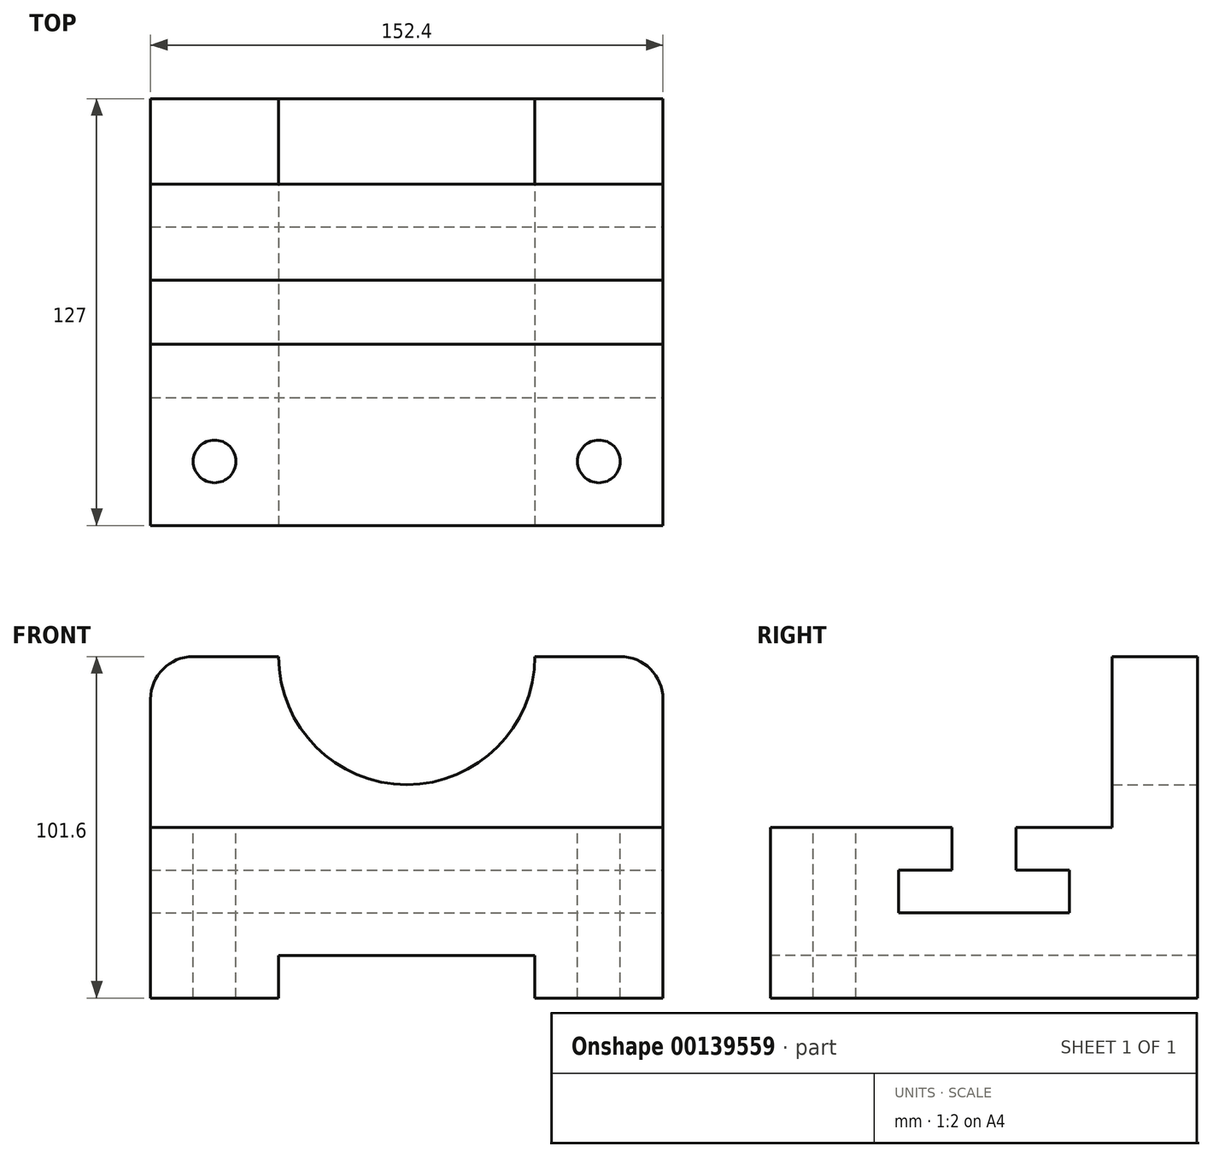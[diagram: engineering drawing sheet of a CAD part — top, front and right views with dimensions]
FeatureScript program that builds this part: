
annotation { "Feature Type Name" : "Feature", "Feature Type Description" : "" }
export const myFeature = defineFeature(function(context is Context, id is Id, definition is map)
    precondition{}
    {
        {
            var Q0;
            Q0=qCreatedBy(makeId("Front.planeOp"),FACE);
            var sketch = newSketch(context, id + "F0", { "sketchPlane" : qUnion([Q0])});
            skLineSegment(sketch, "E0", {"start": v(0, 0) * mm, "end": v(76.2, 0) * mm});
            skLineSegment(sketch, "E1.MirrorCS", {"start": v(0, 0) * mm, "end": v(-76.2, 0) * mm});
            skLineSegment(sketch, "E2", {"start": v(-76.2, 0) * mm, "end": v(-76.2, 101.6) * mm});
            skLineSegment(sketch, "E3.MirrorCS", {"start": v(76.2, 0) * mm, "end": v(76.2, 101.6) * mm});
            skLineSegment(sketch, "E4", {"start": v(-76.2, 101.6) * mm, "end": v(76.2, 101.6) * mm});
            skSolve(sketch);
        }
        {
            var Q0;
            Q0 = qSketchRegion(id + "F0", true);
            extrude(context, id + "F1", {"entities" : qUnion([Q0]), "endBound" : BoundingType.SYMMETRIC, "oppositeDirection" : true, "depth" : 127 * mm});
        }
        {
            var Q0;
            Q0=makeQuery(id+"F1.opExtrude","CAP_FACE",FACE,{"disambiguationData":[OSD([sQuery(id+"F0.wireOp",EDGE,"E0"),sQuery(id+"F0.wireOp",EDGE,"E1.MirrorCS"),sQuery(id+"F0.wireOp",EDGE,"E2"),sQuery(id+"F0.wireOp",EDGE,"E3.MirrorCS"),sQuery(id+"F0.wireOp",EDGE,"E4")])],"isStart":true});
            var sketch = newSketch(context, id + "F2", { "sketchPlane" : qUnion([Q0])});
            skLineSegment(sketch, "E5.0", {"start": v(-76.2, 50.8) * mm, "end": v(-76.2, 101.6) * mm});
            skLineSegment(sketch, "E5.1", {"start": v(-76.2, 101.6) * mm, "end": v(76.2, 101.6) * mm});
            skLineSegment(sketch, "E5.2", {"start": v(76.2, 50.8) * mm, "end": v(76.2, 101.6) * mm});
            skPoint(sketch, "E6", {"position": v(-76.2, 50.8) * mm});
            skPoint(sketch, "E7.orphan", {"position": v(-76.2, 0) * mm});
            skLineSegment(sketch, "E8", {"start": v(-76.2, 50.8) * mm, "end": v(76.2, 50.8) * mm});
            skPoint(sketch, "E9.orphan", {"position": v(76.2, 0) * mm});
            skSolve(sketch);
        }
        {
            var Q0;
            Q0=makeQuery(id+"F2.imprint","IMPRINT",FACE,{"disambiguationData":[TD([[makeQuery(id+"F2.imprint","IMPRINT",EDGE,{"derivedFrom":sQuery(id+"F2.wireOp",EDGE,"E5.0")}),-1.0]])]});
            extrude(context, id + "F3", {"entities" : qUnion([Q0]), "operationType" : NewBodyOperationType.REMOVE, "oppositeDirection" : true, "depth" : 101.6 * mm});
        }
        {
            var Q0;
            Q0=makeQuery(id+"F1.opExtrude","CAP_FACE",FACE,{"disambiguationData":[OSD([sQuery(id+"F0.wireOp",EDGE,"E0"),sQuery(id+"F0.wireOp",EDGE,"E1.MirrorCS"),sQuery(id+"F0.wireOp",EDGE,"E2"),sQuery(id+"F0.wireOp",EDGE,"E3.MirrorCS"),sQuery(id+"F0.wireOp",EDGE,"E4")])],"isStart":true});
            var sketch = newSketch(context, id + "F4", { "sketchPlane" : qUnion([Q0])});
            skLineSegment(sketch, "E10.0", {"start": v(38.1, 0) * mm, "end": v(-38.1, 0) * mm});
            skPoint(sketch, "E11", {"position": v(38.1, 0) * mm});
            skPoint(sketch, "E12.MirrorP", {"position": v(-38.1, 0) * mm});
            skPoint(sketch, "E13.orphan", {"position": v(-76.2, 0) * mm});
            skPoint(sketch, "E14.orphan", {"position": v(76.2, 0) * mm});
            skLineSegment(sketch, "E15", {"start": v(-38.1, 0) * mm, "end": v(-38.1, 12.7) * mm});
            skLineSegment(sketch, "E16", {"start": v(-38.1, 12.7) * mm, "end": v(38.1, 12.7) * mm});
            skLineSegment(sketch, "E17", {"start": v(38.1, 12.7) * mm, "end": v(38.1, 0) * mm});
            skSolve(sketch);
        }
        {
            var Q0;
            Q0=makeQuery(id+"F4.imprint","IMPRINT",FACE,{"disambiguationData":[TD([[makeQuery(id+"F4.imprint","IMPRINT",EDGE,{"derivedFrom":sQuery(id+"F4.wireOp",EDGE,"E10.0")}),-1.0]])]});
            extrude(context, id + "F5", {"entities" : qUnion([Q0]), "operationType" : NewBodyOperationType.REMOVE, "oppositeDirection" : true, "depth" : 127 * mm});
        }
        {
            var Q0;
            Q0=makeQuery(id+"F1.opExtrude","SWEPT_FACE",FACE,{"disambiguationData":[OSD([sQuery(id+"F0.wireOp",EDGE,"E3.MirrorCS")])]});
            var sketch = newSketch(context, id + "F6", { "sketchPlane" : qUnion([Q0])});
            skLineSegment(sketch, "E18.0", {"start": v(9.53, 50.8) * mm, "end": v(-9.52, 50.8) * mm});
            skPoint(sketch, "E19", {"position": v(-9.53, 50.8) * mm});
            skPoint(sketch, "E20", {"position": v(9.52, 50.8) * mm});
            skLineSegment(sketch, "E21", {"start": v(9.52, 50.8) * mm, "end": v(9.52, 38.1) * mm});
            skLineSegment(sketch, "E22", {"start": v(-9.53, 50.8) * mm, "end": v(-9.53, 38.1) * mm});
            skLineSegment(sketch, "E23", {"start": v(-9.53, 38.1) * mm, "end": v(-25.4, 38.1) * mm});
            skLineSegment(sketch, "E24", {"start": v(-25.4, 38.1) * mm, "end": v(-25.4, 25.4) * mm});
            skLineSegment(sketch, "E25", {"start": v(-25.4, 25.4) * mm, "end": v(25.4, 25.4) * mm});
            skLineSegment(sketch, "E26", {"start": v(25.4, 25.4) * mm, "end": v(25.4, 38.1) * mm});
            skLineSegment(sketch, "E27", {"start": v(9.52, 38.1) * mm, "end": v(25.4, 38.1) * mm});
            skPoint(sketch, "E28.orphan", {"position": v(-63.5, 50.8) * mm});
            skPoint(sketch, "E29.orphan", {"position": v(38.1, 50.8) * mm});
            skSolve(sketch);
        }
        {
            var Q0;
            Q0=makeQuery(id+"F6.imprint","IMPRINT",FACE,{"disambiguationData":[TD([[makeQuery(id+"F6.imprint","IMPRINT",EDGE,{"derivedFrom":sQuery(id+"F6.wireOp",EDGE,"E18.0")}),1.0]])]});
            extrude(context, id + "F7", {"entities" : qUnion([Q0]), "operationType" : NewBodyOperationType.REMOVE, "oppositeDirection" : true, "depth" : 152.4 * mm});
        }
        {
            var Q0;
            Q0=makeQuery(id+"F7.boolean.opBoolean","SPLIT",FACE,{"disambiguationData":[TD([makeQuery(id+"F7.opExtrude","SWEPT_FACE",FACE,{"disambiguationData":[OSD([sQuery(id+"F6.wireOp",EDGE,"E22")])]})])],"derivedFrom":makeQuery(id+"F3.boolean.opBoolean","COPY",FACE,{"derivedFrom":makeQuery(id+"F3.opExtrude","SWEPT_FACE",FACE,{"disambiguationData":[OSD([sQuery(id+"F2.wireOp",EDGE,"E8")])]})})});
            var sketch = newSketch(context, id + "F8", { "sketchPlane" : qUnion([Q0])});
            skCircle(sketch, "E30", {"center": v(-57.15, -44.45) * mm, "radius": 6.35 * mm});
            skCircle(sketch, "E31.MirrorC", {"center": v(57.15, -44.45) * mm, "radius": 6.35 * mm});
            skSolve(sketch);
        }
        {
            var Q0;
            Q0 = qSketchRegion(id + "F8", true);
            extrude(context, id + "F9", {"entities" : qUnion([Q0]), "operationType" : NewBodyOperationType.REMOVE, "oppositeDirection" : true, "depth" : 50.8 * mm});
        }
        {
            var Q0;
            Q0=makeQuery(id+"F1.opExtrude","CAP_FACE",FACE,{"disambiguationData":[OSD([sQuery(id+"F0.wireOp",EDGE,"E0"),sQuery(id+"F0.wireOp",EDGE,"E1.MirrorCS"),sQuery(id+"F0.wireOp",EDGE,"E2"),sQuery(id+"F0.wireOp",EDGE,"E3.MirrorCS"),sQuery(id+"F0.wireOp",EDGE,"E4")])],"isStart":false});
            var sketch = newSketch(context, id + "F10", { "sketchPlane" : qUnion([Q0])});
            skLineSegment(sketch, "E32.0", {"start": v(63.5, 101.6) * mm, "end": v(-63.5, 101.6) * mm});
            skArc(sketch, "E33", {"start": v(-38.1, 101.6) * mm, "mid": v(0, 63.5) * mm, "end": v(38.1, 101.6) * mm});
            skPoint(sketch, "E34.visualSharp", {"position": v(76.2, 101.6) * mm});
            skArc(sketch, "E34.filletArc", {"start": v(76.2, 88.9) * mm, "mid": v(72.48, 97.88) * mm, "end": v(63.5, 101.6) * mm});
            skPoint(sketch, "E35.visualSharp", {"position": v(-76.2, 101.6) * mm});
            skArc(sketch, "E35.filletArc", {"start": v(-63.5, 101.6) * mm, "mid": v(-72.48, 97.88) * mm, "end": v(-76.2, 88.9) * mm});
            skPoint(sketch, "E36.0.start.orphan", {"position": v(-76.2, 0) * mm});
            skPoint(sketch, "E37.0.start.orphan", {"position": v(76.2, 0) * mm});
            skLineSegment(sketch, "E38", {"start": v(-76.2, 88.9) * mm, "end": v(-76.2, 101.6) * mm});
            skLineSegment(sketch, "E39", {"start": v(-76.2, 101.6) * mm, "end": v(-63.5, 101.6) * mm});
            skLineSegment(sketch, "E40", {"start": v(63.5, 101.6) * mm, "end": v(76.2, 101.6) * mm});
            skLineSegment(sketch, "E41", {"start": v(76.2, 88.9) * mm, "end": v(76.2, 101.6) * mm});
            skSolve(sketch);
        }
        {
            var Q0;
            Q0=makeQuery(id+"F10.imprint","IMPRINT",FACE,{"disambiguationData":[TD([[makeQuery(id+"F10.imprint","IMPRINT",EDGE,{"derivedFrom":sQuery(id+"F10.wireOp",EDGE,"E34.filletArc")}),-1.0]])]});
            extrude(context, id + "F11", {"entities" : qUnion([Q0]), "operationType" : NewBodyOperationType.REMOVE, "oppositeDirection" : true, "depth" : 25.4 * mm});
        }
        {
            var Q0;
            Q0=makeQuery(id+"F10.imprint","IMPRINT",FACE,{"disambiguationData":[TD([[makeQuery(id+"F10.imprint","IMPRINT",EDGE,{"derivedFrom":sQuery(id+"F10.wireOp",EDGE,"E35.filletArc")}),-1.0]])]});
            extrude(context, id + "F12", {"entities" : qUnion([Q0]), "operationType" : NewBodyOperationType.REMOVE, "oppositeDirection" : true, "depth" : 25.4 * mm});
        }
        {
            var Q0;
            {var subQ0=sQuery(id+"F10.wireOp",EDGE,"E33");Q0=makeQuery(id+"F10.imprint","IMPRINT",FACE,{"disambiguationData":[TD([[makeQuery(id+"F10.imprint","IMPRINT",EDGE,{"derivedFrom":subQ0}),1.0]])]});}
            extrude(context, id + "F13", {"entities" : qUnion([Q0]), "operationType" : NewBodyOperationType.REMOVE, "oppositeDirection" : true, "depth" : 25.4 * mm});
        }
    });
